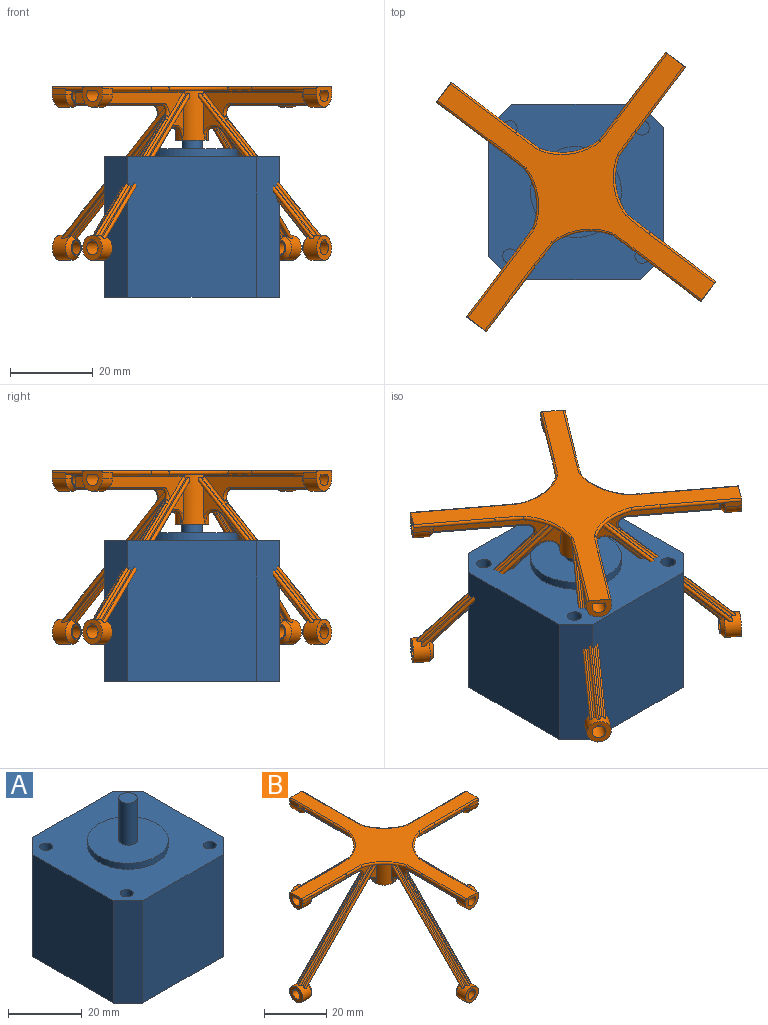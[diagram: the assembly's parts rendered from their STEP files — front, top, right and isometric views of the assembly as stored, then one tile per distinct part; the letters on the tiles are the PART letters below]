
ASSEMBLY  parts=2 mates=1
PART A: 22 faces, bbox 42.3x42.3x50 mm
  f0: plane 42.3x42.3mm, normal (0,0,1), area 1306.8mm2, adj f1,f2,f3,f4,f6,f10,f11,f12
  f1: plane 34x31mm, normal (0,-1,0), area 1054mm2, adj f0,f5,f10,f11
  f2: plane 34x31mm, normal (1,0,0), area 1054mm2, adj f0,f5,f11,f13
  f3: plane 34x31mm, normal (0,1,0), area 1054mm2, adj f0,f5,f12,f13
  f4: plane 34x31mm, normal (-1,0,0), area 1054mm2, adj f0,f5,f10,f12
  f5: plane 42.3x42.3mm, normal (0,0,-1), area 1725.4mm2, adj f1,f2,f3,f4,f10,f11,f12,f13
  f6: cylinder r=11mm len=22mm, axis (0,0,-1), area 138.2mm2, adj f0,f7
  f7: plane 22x22mm, normal (0,0,1), area 360.5mm2, adj f6,f8
  f8: cylinder r=2.5mm len=14mm, axis (0,0,-1), area 219.9mm2, adj f7,f9
  f9: plane 5x5mm, normal (0,0,1), area 19.6mm2, adj f8
  f10: plane 34x5.65mm, normal (-0.71,-0.71,0), area 271.7mm2, adj f0,f1,f4,f5
  f11: plane 34x5.65mm, normal (0.71,-0.71,0), area 271.7mm2, adj f0,f1,f2,f5
  f12: plane 34x5.65mm, normal (-0.71,0.71,0), area 271.7mm2, adj f0,f3,f4,f5
  f13: plane 34x5.65mm, normal (0.71,0.71,0), area 271.7mm2, adj f0,f2,f3,f5
  f14: cylinder r=1.75mm len=4.5mm, axis (0,0,1), area 49.5mm2, adj f0,f15
  f15: plane 3.5x3.5mm, normal (0,0,1), area 9.6mm2, adj f14
  f16: cylinder r=1.75mm len=4.5mm, axis (0,0,1), area 49.5mm2, adj f0,f17
  f17: plane 3.5x3.5mm, normal (0,0,1), area 9.6mm2, adj f16
  f18: cylinder r=1.75mm len=4.5mm, axis (0,0,1), area 49.5mm2, adj f0,f19
  f19: plane 3.5x3.5mm, normal (0,0,1), area 9.6mm2, adj f18
  f20: cylinder r=1.75mm len=4.5mm, axis (0,0,1), area 49.5mm2, adj f0,f21
  f21: plane 3.5x3.5mm, normal (0,0,1), area 9.6mm2, adj f20
PART B: 214 faces, bbox 81x81x43 mm
  f0: cylinder r=4mm len=12mm, axis (0,0,-1), area 239.3mm2, adj f6,f7,f8,f9,f13,f16,f17,f18
  f1: plane 2.7x2mm, normal (1,0,0), area 2.8mm2, adj f2,f10,f11,f18,f30,f32
  f2: cylinder r=1.7mm len=5mm, axis (1,0,0), area 37.4mm2, adj f1,f3,f15,f18,f21
  f3: plane 2.94x1.5mm, normal (-1,0,0), area 1.1mm2, adj f2,f11,f18,f51,f52
  f4: plane 1.01x0.38mm, normal (1,0,0), area 0.3mm2, adj f23,f28
  f5: plane 0.15x0.02mm, normal (-0.71,0,-0.7), area 0mm2, adj f22,f23,f26
  f6: plane 33.05x31.83mm, normal (0,-1,0), area 34.7mm2, adj f0,f24,f33,f45,f46,f54
  f7: plane 33.05x31.83mm, normal (0,1,0), area 34.7mm2, adj f0,f24,f34,f45,f46,f54
  f8: plane 34.78x34.32mm, normal (0.71,0,0.7), area 24.3mm2, adj f0,f22,f29,f48
  f9: plane 34.78x34.32mm, normal (0.71,0,0.7), area 24.3mm2, adj f0,f22,f31,f47
  f10: plane 30.79x5.75mm, normal (0,-1,0), area 80mm2, adj f1,f21,f29,f30,f42,f44,f52
  f11: plane 30.79x5.75mm, normal (0,1,0), area 80mm2, adj f1,f3,f31,f32,f42,f44,f52
  f12: plane 80x80mm, normal (0,0,1), area 932.8mm2, adj f15,f35,f36,f37,f38,f57,f58,f59
  f13: plane 8x8mm, normal (0,0,-1), area 23.8mm2, adj f0,f55
  f14: plane 28.28x28.28mm, normal (0.71,0,0.71), area 1.1mm2, adj f19,f22,f39,f41
  f15: plane 6x5mm, normal (1,0,0), area 18.3mm2, adj f2,f12,f18,f20,f35,f36,f49,f50
  f16: plane 33.36x32.92mm, normal (-0.71,0,-0.7), area 23.3mm2, adj f0,f22,f33,f48
  f17: plane 33.36x32.92mm, normal (-0.71,0,-0.7), area 23.3mm2, adj f0,f22,f34,f47
  f18: plane 80x80mm, normal (0,0,-1), area 590.2mm2, adj f0,f1,f2,f3,f15,f21,f30,f32
  f19: cylinder r=2mm len=0.81mm, axis (0,1,0), area 0mm2, adj f14,f40,f43
  f20: cylinder r=3mm len=6mm, axis (1,0,0), area 38mm2, adj f15,f49,f50,f52
  f21: plane 2.94x1.5mm, normal (-1,0,0), area 1.1mm2, adj f2,f10,f18,f52,f53
  f22: cylinder r=3mm len=6mm, axis (1,0,0), area 68.3mm2, adj f5,f8,f9,f14,f16,f17,f23,f25
  f23: plane 6.02x6.02mm, normal (1,0,0), area 18.9mm2, adj f4,f5,f22,f25,f26,f27,f28
  f24: plane 5.81x5.01mm, normal (-1,0,0), area 3.7mm2, adj f6,f7,f28,f45,f54
  f25: plane 0.15x0.02mm, normal (-0.71,0,-0.7), area 0mm2, adj f22,f23,f27
  f26: plane 0.02x0.02mm, normal (0,1,0), area 0mm2, adj f5,f22,f23
  f27: plane 0.02x0.02mm, normal (0,-1,0), area 0mm2, adj f22,f23,f25
  f28: cylinder r=1.7mm len=5mm, axis (1,0,0), area 53.4mm2, adj f4,f23,f24
  f29: cylinder r=0.5mm len=35.1mm, axis (0.7,0,-0.71), area 35.2mm2, adj f0,f8,f10,f22,f30,f41,f43
  f30: cylinder r=0.5mm len=31.13mm, axis (-1,0,0), area 24.4mm2, adj f0,f1,f10,f18,f29
  f31: cylinder r=0.5mm len=35.1mm, axis (-0.7,0,0.71), area 35.2mm2, adj f0,f9,f11,f22,f32,f39,f40
  f32: cylinder r=0.5mm len=31.13mm, axis (1,0,0), area 24.4mm2, adj f0,f1,f11,f18,f31
  f33: cylinder r=0.5mm len=33.29mm, axis (-0.7,0,0.71), area 35.9mm2, adj f0,f6,f16,f22,f54
  f34: cylinder r=0.5mm len=33.29mm, axis (0.7,0,-0.71), area 35.9mm2, adj f0,f7,f17,f22,f54
  f35: cylinder r=0.5mm len=19.83mm, axis (1,0,0), area 27.8mm2, adj f12,f15,f18,f37,f49,f51
  f36: cylinder r=0.5mm len=19.83mm, axis (-1,0,0), area 27.8mm2, adj f12,f15,f18,f38,f50,f53
  f37: torus R=200.5mm, axis (0,0,1), area 11mm2, adj f12,f18,f35,f61
  f38: torus R=200.5mm, axis (0,0,1), area 11mm2, adj f12,f18,f36,f163
  f39: bspline ~28.44x28.34mm, area 28.2mm2, adj f14,f22,f31,f40
  f40: bspline ~1.24x1.09mm, area 0.7mm2, adj f19,f31,f39,f42
  f41: bspline ~28.44x28.34mm, area 28.2mm2, adj f14,f22,f29,f43
  f42: torus R=2.5mm, axis (0,-1,0), area 6.4mm2, adj f10,f11,f40,f43,f44
  f43: bspline ~1.5x1.23mm, area 0.7mm2, adj f19,f29,f41,f42
  f44: cylinder r=0.5mm len=22.73mm, axis (1,0,0), area 35.7mm2, adj f10,f11,f42,f52
  f45: cylinder r=0.5mm len=26.2mm, axis (-0.7,0,0.71), area 57mm2, adj f6,f7,f24,f46
  f46: torus R=3.5mm, axis (0,-1,0), area 10.5mm2, adj f0,f6,f7,f45
  f47: cylinder r=0.5mm len=35.47mm, axis (-0.7,0,0.71), area 75.5mm2, adj f0,f9,f17,f22
  f48: cylinder r=0.5mm len=35.47mm, axis (0.7,0,-0.71), area 75.5mm2, adj f0,f8,f16,f22
  f49: cylinder r=50mm len=4mm, axis (-1,0,0), area 5.8mm2, adj f15,f20,f35,f51
  f50: cylinder r=50mm len=4mm, axis (1,0,0), area 5.8mm2, adj f15,f20,f36,f53
  f51: cone r=51mm half-angle=45deg, axis (-1,0,0), area 1.5mm2, adj f3,f18,f35,f49,f52
  f52: cone r=3mm half-angle=45deg, axis (1,0,0), area 10.6mm2, adj f3,f10,f11,f20,f21,f44,f51,f53
  f53: cone r=51mm half-angle=45deg, axis (-1,0,0), area 1.5mm2, adj f18,f21,f36,f50,f52
  f54: cone r=3mm half-angle=45deg, axis (1,0,0), area 20.7mm2, adj f6,f7,f22,f24,f33,f34
  f55: cylinder r=2.9mm len=12mm, axis (0,0,-1), area 218.7mm2, adj f13,f56
  f56: plane 5.8x5.8mm, normal (0,0,-1), area 26.4mm2, adj f55
  f57: plane 6x5mm, normal (0,-1,0), area 18.3mm2, adj f12,f18,f166,f180,f195,f196,f208,f209
  f58: plane 6x5mm, normal (-1,0,0), area 18.3mm2, adj f12,f18,f63,f77,f92,f93,f106,f107
  f59: plane 6x5mm, normal (0,1,0), area 18.3mm2, adj f12,f18,f117,f118,f131,f132,f147,f161
  f60: torus R=15.5mm, axis (0,0,1), area 23.9mm2, adj f12,f18,f94,f164
  f61: torus R=15.5mm, axis (0,0,1), area 23.9mm2, adj f12,f18,f37,f129
  f62: plane 2.7x2mm, normal (-1,0,0), area 2.8mm2, adj f18,f63,f71,f72,f87,f89
  f63: cylinder r=1.7mm len=5mm, axis (-1,0,0), area 37.4mm2, adj f18,f58,f62,f64,f78
  f64: plane 2.94x1.5mm, normal (1,0,0), area 1.1mm2, adj f18,f63,f72,f108,f109
  f65: plane 1.01x0.38mm, normal (-1,0,0), area 0.3mm2, adj f80,f85
  f66: plane 0.15x0.02mm, normal (0.71,0,-0.7), area 0mm2, adj f79,f80,f83
  f67: plane 33.05x31.83mm, normal (0,1,0), area 34.7mm2, adj f0,f81,f90,f102,f103,f111
  f68: plane 33.05x31.83mm, normal (0,-1,0), area 34.7mm2, adj f0,f81,f91,f102,f103,f111
  f69: plane 34.78x34.32mm, normal (-0.71,0,0.7), area 24.3mm2, adj f0,f79,f86,f105
  f70: plane 34.78x34.32mm, normal (-0.71,0,0.7), area 24.3mm2, adj f0,f79,f88,f104
  f71: plane 30.79x5.75mm, normal (0,1,0), area 80mm2, adj f62,f78,f86,f87,f99,f101,f109
  f72: plane 30.79x5.75mm, normal (0,-1,0), area 80mm2, adj f62,f64,f88,f89,f99,f101,f109
  f73: plane 28.28x28.28mm, normal (-0.71,0,0.71), area 1.1mm2, adj f76,f79,f96,f98
  f74: plane 33.36x32.92mm, normal (0.71,0,-0.7), area 23.3mm2, adj f0,f79,f90,f105
  f75: plane 33.36x32.92mm, normal (0.71,0,-0.7), area 23.3mm2, adj f0,f79,f91,f104
  f76: cylinder r=2mm len=0.81mm, axis (0,-1,0), area 0mm2, adj f73,f97,f100
  f77: cylinder r=3mm len=6mm, axis (-1,0,0), area 38mm2, adj f58,f106,f107,f109
  f78: plane 2.94x1.5mm, normal (1,0,0), area 1.1mm2, adj f18,f63,f71,f109,f110
  f79: cylinder r=3mm len=6mm, axis (-1,0,0), area 68.3mm2, adj f66,f69,f70,f73,f74,f75,f80,f82
  f80: plane 6.02x6.02mm, normal (-1,0,0), area 18.9mm2, adj f65,f66,f79,f82,f83,f84,f85
  f81: plane 5.81x5.01mm, normal (1,0,0), area 3.7mm2, adj f67,f68,f85,f102,f111
  f82: plane 0.15x0.02mm, normal (0.71,0,-0.7), area 0mm2, adj f79,f80,f84
  f83: plane 0.02x0.02mm, normal (0,-1,0), area 0mm2, adj f66,f79,f80
  f84: plane 0.02x0.02mm, normal (0,1,0), area 0mm2, adj f79,f80,f82
  f85: cylinder r=1.7mm len=5mm, axis (-1,0,0), area 53.4mm2, adj f65,f80,f81
  f86: cylinder r=0.5mm len=35.1mm, axis (-0.7,0,-0.71), area 35.2mm2, adj f0,f69,f71,f79,f87,f98,f100
  f87: cylinder r=0.5mm len=31.13mm, axis (1,0,0), area 24.4mm2, adj f0,f18,f62,f71,f86
  f88: cylinder r=0.5mm len=35.1mm, axis (0.7,0,0.71), area 35.2mm2, adj f0,f70,f72,f79,f89,f96,f97
  f89: cylinder r=0.5mm len=31.13mm, axis (-1,0,0), area 24.4mm2, adj f0,f18,f62,f72,f88
  f90: cylinder r=0.5mm len=33.29mm, axis (0.7,0,0.71), area 35.9mm2, adj f0,f67,f74,f79,f111
  f91: cylinder r=0.5mm len=33.29mm, axis (-0.7,0,-0.71), area 35.9mm2, adj f0,f68,f75,f79,f111
  f92: cylinder r=0.5mm len=19.83mm, axis (-1,0,0), area 27.8mm2, adj f12,f18,f58,f94,f106,f108
  f93: cylinder r=0.5mm len=19.83mm, axis (1,0,0), area 27.8mm2, adj f12,f18,f58,f95,f107,f110
  f94: torus R=200.5mm, axis (0,0,1), area 11mm2, adj f12,f18,f60,f92
  f95: torus R=200.5mm, axis (0,0,1), area 11mm2, adj f12,f18,f93,f112
  f96: bspline ~28.44x28.34mm, area 28.2mm2, adj f73,f79,f88,f97
  f97: bspline ~1.24x1.09mm, area 0.7mm2, adj f76,f88,f96,f99
  f98: bspline ~28.44x28.34mm, area 28.2mm2, adj f73,f79,f86,f100
  f99: torus R=2.5mm, axis (0,1,0), area 6.4mm2, adj f71,f72,f97,f100,f101
  f100: bspline ~1.5x1.23mm, area 0.7mm2, adj f76,f86,f98,f99
  f101: cylinder r=0.5mm len=22.73mm, axis (-1,0,0), area 35.7mm2, adj f71,f72,f99,f109
  f102: cylinder r=0.5mm len=26.2mm, axis (0.7,0,0.71), area 57mm2, adj f67,f68,f81,f103
  f103: torus R=3.5mm, axis (0,1,0), area 10.5mm2, adj f0,f67,f68,f102
  f104: cylinder r=0.5mm len=35.47mm, axis (0.7,0,0.71), area 75.5mm2, adj f0,f70,f75,f79
  f105: cylinder r=0.5mm len=35.47mm, axis (-0.7,0,-0.71), area 75.5mm2, adj f0,f69,f74,f79
  f106: cylinder r=50mm len=4mm, axis (1,0,0), area 5.8mm2, adj f58,f77,f92,f108
  f107: cylinder r=50mm len=4mm, axis (-1,0,0), area 5.8mm2, adj f58,f77,f93,f110
  f108: cone r=51mm half-angle=45deg, axis (1,0,0), area 1.5mm2, adj f18,f64,f92,f106,f109
  f109: cone r=3mm half-angle=45deg, axis (-1,0,0), area 10.6mm2, adj f64,f71,f72,f77,f78,f101,f108,f110
  f110: cone r=51mm half-angle=45deg, axis (1,0,0), area 1.5mm2, adj f18,f78,f93,f107,f109
  f111: cone r=3mm half-angle=45deg, axis (-1,0,0), area 20.7mm2, adj f67,f68,f79,f81,f90,f91
  f112: torus R=15.5mm, axis (0,0,1), area 23.9mm2, adj f12,f18,f95,f130
  f113: cone r=3mm half-angle=45deg, axis (0,1,0), area 20.7mm2, adj f133,f134,f143,f145,f156,f157
  f114: cone r=51mm half-angle=45deg, axis (0,-1,0), area 1.5mm2, adj f18,f115,f117,f131,f146
  f115: cone r=3mm half-angle=45deg, axis (0,1,0), area 10.6mm2, adj f114,f116,f123,f146,f147,f152,f153,f160
  f116: cone r=51mm half-angle=45deg, axis (0,-1,0), area 1.5mm2, adj f18,f115,f118,f132,f160
  f117: cylinder r=50mm len=4mm, axis (0,1,0), area 5.8mm2, adj f59,f114,f131,f147
  f118: cylinder r=50mm len=4mm, axis (0,-1,0), area 5.8mm2, adj f59,f116,f132,f147
  f119: cylinder r=0.5mm len=35.47mm, axis (0,0.7,-0.71), area 75.5mm2, adj f0,f145,f150,f155
  f120: cylinder r=0.5mm len=35.47mm, axis (0,-0.7,0.71), area 75.5mm2, adj f0,f145,f149,f154
  f121: torus R=3.5mm, axis (1,0,0), area 10.5mm2, adj f0,f122,f156,f157
  f122: cylinder r=0.5mm len=26.2mm, axis (0,-0.7,0.71), area 57mm2, adj f121,f143,f156,f157
  f123: cylinder r=0.5mm len=22.73mm, axis (0,1,0), area 35.7mm2, adj f115,f125,f152,f153
  f124: bspline ~1.5x1.23mm, area 0.7mm2, adj f125,f126,f138,f148
  f125: torus R=2.5mm, axis (1,0,0), area 6.4mm2, adj f123,f124,f127,f152,f153
  f126: bspline ~28.44x28.34mm, area 28.2mm2, adj f124,f138,f145,f151
  f127: bspline ~1.24x1.09mm, area 0.7mm2, adj f125,f128,f136,f148
  f128: bspline ~28.44x28.34mm, area 28.2mm2, adj f127,f136,f145,f151
  f129: torus R=200.5mm, axis (0,0,1), area 11mm2, adj f12,f18,f61,f131
  f130: torus R=200.5mm, axis (0,0,1), area 11mm2, adj f12,f18,f112,f132
  f131: cylinder r=0.5mm len=19.83mm, axis (0,-1,0), area 27.8mm2, adj f12,f18,f59,f114,f117,f129
  f132: cylinder r=0.5mm len=19.83mm, axis (0,1,0), area 27.8mm2, adj f12,f18,f59,f116,f118,f130
  f133: cylinder r=0.5mm len=33.29mm, axis (0,0.7,-0.71), area 35.9mm2, adj f0,f113,f145,f149,f156
  f134: cylinder r=0.5mm len=33.29mm, axis (0,-0.7,0.71), area 35.9mm2, adj f0,f113,f145,f150,f157
  f135: cylinder r=0.5mm len=31.13mm, axis (0,1,0), area 24.4mm2, adj f0,f18,f136,f152,f162
  f136: cylinder r=0.5mm len=35.1mm, axis (0,-0.7,0.71), area 35.2mm2, adj f0,f127,f128,f135,f145,f152,f154
  f137: cylinder r=0.5mm len=31.13mm, axis (0,-1,0), area 24.4mm2, adj f0,f18,f138,f153,f162
  f138: cylinder r=0.5mm len=35.1mm, axis (0,0.7,-0.71), area 35.2mm2, adj f0,f124,f126,f137,f145,f153,f155
  f139: cylinder r=1.7mm len=5mm, axis (0,1,0), area 53.4mm2, adj f143,f144,f159
  f140: plane 0.02x0.02mm, normal (1,0,0), area 0mm2, adj f142,f144,f145
  f141: plane 0.02x0.02mm, normal (-1,0,0), area 0mm2, adj f144,f145,f158
  f142: plane 0.15x0.02mm, normal (0,-0.71,-0.7), area 0mm2, adj f140,f144,f145
  f143: plane 5.81x5.01mm, normal (0,-1,0), area 3.7mm2, adj f113,f122,f139,f156,f157
  f144: plane 6.02x6.02mm, normal (0,1,0), area 18.9mm2, adj f139,f140,f141,f142,f145,f158,f159
  f145: cylinder r=3mm len=6mm, axis (0,1,0), area 68.3mm2, adj f113,f119,f120,f126,f128,f133,f134,f136
  f146: plane 2.94x1.5mm, normal (0,-1,0), area 1.1mm2, adj f18,f114,f115,f153,f161
  f147: cylinder r=3mm len=6mm, axis (0,1,0), area 38mm2, adj f59,f115,f117,f118
  f148: cylinder r=2mm len=0.81mm, axis (-1,0,0), area 0mm2, adj f124,f127,f151
  f149: plane 33.36x32.92mm, normal (0,-0.71,-0.7), area 23.3mm2, adj f0,f120,f133,f145
  f150: plane 33.36x32.92mm, normal (0,-0.71,-0.7), area 23.3mm2, adj f0,f119,f134,f145
  f151: plane 28.28x28.28mm, normal (0,0.71,0.71), area 1.1mm2, adj f126,f128,f145,f148
  f152: plane 30.79x5.75mm, normal (-1,0,0), area 80mm2, adj f115,f123,f125,f135,f136,f160,f162
  f153: plane 30.79x5.75mm, normal (1,0,0), area 80mm2, adj f115,f123,f125,f137,f138,f146,f162
  f154: plane 34.78x34.32mm, normal (0,0.71,0.7), area 24.3mm2, adj f0,f120,f136,f145
  f155: plane 34.78x34.32mm, normal (0,0.71,0.7), area 24.3mm2, adj f0,f119,f138,f145
  f156: plane 33.05x31.83mm, normal (-1,0,0), area 34.7mm2, adj f0,f113,f121,f122,f133,f143
  f157: plane 33.05x31.83mm, normal (1,0,0), area 34.7mm2, adj f0,f113,f121,f122,f134,f143
  f158: plane 0.15x0.02mm, normal (0,-0.71,-0.7), area 0mm2, adj f141,f144,f145
  f159: plane 1.01x0.38mm, normal (0,1,0), area 0.3mm2, adj f139,f144
  f160: plane 2.94x1.5mm, normal (0,-1,0), area 1.1mm2, adj f18,f115,f116,f152,f161
  f161: cylinder r=1.7mm len=5mm, axis (0,1,0), area 37.4mm2, adj f18,f59,f146,f160,f162
  f162: plane 2.7x2mm, normal (0,1,0), area 2.8mm2, adj f18,f135,f137,f152,f153,f161
  f163: torus R=15.5mm, axis (0,0,1), area 23.9mm2, adj f12,f18,f38,f197
  f164: torus R=200.5mm, axis (0,0,1), area 11mm2, adj f12,f18,f60,f196
  f165: plane 2.7x2mm, normal (0,-1,0), area 2.8mm2, adj f18,f166,f174,f175,f190,f192
  f166: cylinder r=1.7mm len=5mm, axis (0,-1,0), area 37.4mm2, adj f18,f57,f165,f167,f181
  f167: plane 2.94x1.5mm, normal (0,1,0), area 1.1mm2, adj f18,f166,f175,f210,f211
  f168: plane 1.01x0.38mm, normal (0,-1,0), area 0.3mm2, adj f183,f188
  f169: plane 0.15x0.02mm, normal (0,0.71,-0.7), area 0mm2, adj f182,f183,f186
  f170: plane 33.05x31.83mm, normal (-1,0,0), area 34.7mm2, adj f0,f184,f193,f204,f205,f213
  f171: plane 33.05x31.83mm, normal (1,0,0), area 34.7mm2, adj f0,f184,f194,f204,f205,f213
  f172: plane 34.78x34.32mm, normal (0,-0.71,0.7), area 24.3mm2, adj f0,f182,f189,f207
  f173: plane 34.78x34.32mm, normal (0,-0.71,0.7), area 24.3mm2, adj f0,f182,f191,f206
  f174: plane 30.79x5.75mm, normal (-1,0,0), area 80mm2, adj f165,f181,f189,f190,f201,f203,f211
  f175: plane 30.79x5.75mm, normal (1,0,0), area 80mm2, adj f165,f167,f191,f192,f201,f203,f211
  f176: plane 28.28x28.28mm, normal (0,-0.71,0.71), area 1.1mm2, adj f179,f182,f198,f200
  f177: plane 33.36x32.92mm, normal (0,0.71,-0.7), area 23.3mm2, adj f0,f182,f193,f207
  f178: plane 33.36x32.92mm, normal (0,0.71,-0.7), area 23.3mm2, adj f0,f182,f194,f206
  f179: cylinder r=2mm len=0.81mm, axis (1,0,0), area 0mm2, adj f176,f199,f202
  f180: cylinder r=3mm len=6mm, axis (0,-1,0), area 38mm2, adj f57,f208,f209,f211
  f181: plane 2.94x1.5mm, normal (0,1,0), area 1.1mm2, adj f18,f166,f174,f211,f212
  f182: cylinder r=3mm len=6mm, axis (0,-1,0), area 68.3mm2, adj f169,f172,f173,f176,f177,f178,f183,f185
  f183: plane 6.02x6.02mm, normal (0,-1,0), area 18.9mm2, adj f168,f169,f182,f185,f186,f187,f188
  f184: plane 5.81x5.01mm, normal (0,1,0), area 3.7mm2, adj f170,f171,f188,f204,f213
  f185: plane 0.15x0.02mm, normal (0,0.71,-0.7), area 0mm2, adj f182,f183,f187
  f186: plane 0.02x0.02mm, normal (1,0,0), area 0mm2, adj f169,f182,f183
  f187: plane 0.02x0.02mm, normal (-1,0,0), area 0mm2, adj f182,f183,f185
  f188: cylinder r=1.7mm len=5mm, axis (0,-1,0), area 53.4mm2, adj f168,f183,f184
  f189: cylinder r=0.5mm len=35.1mm, axis (0,-0.7,-0.71), area 35.2mm2, adj f0,f172,f174,f182,f190,f200,f202
  f190: cylinder r=0.5mm len=31.13mm, axis (0,1,0), area 24.4mm2, adj f0,f18,f165,f174,f189
  f191: cylinder r=0.5mm len=35.1mm, axis (0,0.7,0.71), area 35.2mm2, adj f0,f173,f175,f182,f192,f198,f199
  f192: cylinder r=0.5mm len=31.13mm, axis (0,-1,0), area 24.4mm2, adj f0,f18,f165,f175,f191
  f193: cylinder r=0.5mm len=33.29mm, axis (0,0.7,0.71), area 35.9mm2, adj f0,f170,f177,f182,f213
  f194: cylinder r=0.5mm len=33.29mm, axis (0,-0.7,-0.71), area 35.9mm2, adj f0,f171,f178,f182,f213
  f195: cylinder r=0.5mm len=19.83mm, axis (0,-1,0), area 27.8mm2, adj f12,f18,f57,f197,f208,f210
  f196: cylinder r=0.5mm len=19.83mm, axis (0,1,0), area 27.8mm2, adj f12,f18,f57,f164,f209,f212
  f197: torus R=200.5mm, axis (0,0,1), area 11mm2, adj f12,f18,f163,f195
  f198: bspline ~28.44x28.34mm, area 28.2mm2, adj f176,f182,f191,f199
  f199: bspline ~1.24x1.09mm, area 0.7mm2, adj f179,f191,f198,f201
  f200: bspline ~28.44x28.34mm, area 28.2mm2, adj f176,f182,f189,f202
  f201: torus R=2.5mm, axis (-1,0,0), area 6.4mm2, adj f174,f175,f199,f202,f203
  f202: bspline ~1.5x1.23mm, area 0.7mm2, adj f179,f189,f200,f201
  f203: cylinder r=0.5mm len=22.73mm, axis (0,-1,0), area 35.7mm2, adj f174,f175,f201,f211
  f204: cylinder r=0.5mm len=26.2mm, axis (0,0.7,0.71), area 57mm2, adj f170,f171,f184,f205
  f205: torus R=3.5mm, axis (-1,0,0), area 10.5mm2, adj f0,f170,f171,f204
  f206: cylinder r=0.5mm len=35.47mm, axis (0,0.7,0.71), area 75.5mm2, adj f0,f173,f178,f182
  f207: cylinder r=0.5mm len=35.47mm, axis (0,-0.7,-0.71), area 75.5mm2, adj f0,f172,f177,f182
  f208: cylinder r=50mm len=4mm, axis (0,1,0), area 5.8mm2, adj f57,f180,f195,f210
  f209: cylinder r=50mm len=4mm, axis (0,-1,0), area 5.8mm2, adj f57,f180,f196,f212
  f210: cone r=51mm half-angle=45deg, axis (0,1,0), area 1.5mm2, adj f18,f167,f195,f208,f211
  f211: cone r=3mm half-angle=45deg, axis (0,-1,0), area 10.6mm2, adj f167,f174,f175,f180,f181,f203,f210,f212
  f212: cone r=51mm half-angle=45deg, axis (0,1,0), area 1.5mm2, adj f18,f181,f196,f209,f211
  f213: cone r=3mm half-angle=45deg, axis (0,-1,0), area 20.7mm2, adj f170,f171,f182,f184,f193,f194
PLACE A at identity
PLACE B rot(axis=(0,0,1),53deg) t=(0,0,38)mm
MATE revolute B.f0 <-> A.f6  axis (0,0,-1) through (0,0,50)mm
